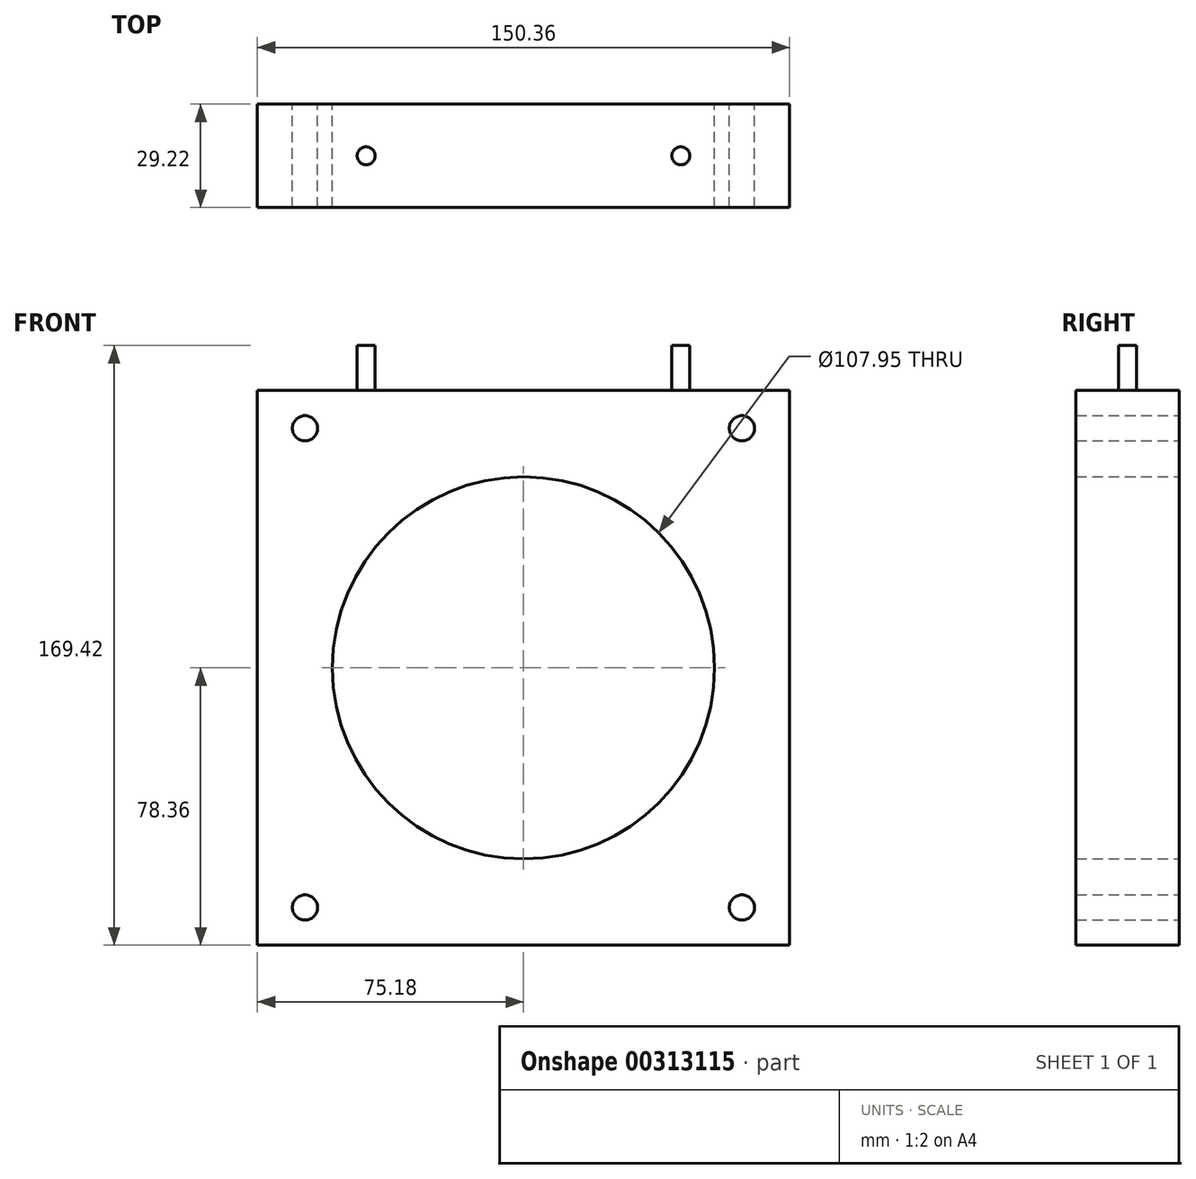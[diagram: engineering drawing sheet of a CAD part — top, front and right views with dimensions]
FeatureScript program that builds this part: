
annotation { "Feature Type Name" : "Feature", "Feature Type Description" : "" }
export const myFeature = defineFeature(function(context is Context, id is Id, definition is map)
    precondition{}
    {
        {
            var Q0;
            Q0=qCreatedBy(makeId("Front.planeOp"),FACE);
            var sketch = newSketch(context, id + "F0", { "sketchPlane" : qUnion([Q0])});
            skLineSegment(sketch, "E0.bottom", {"start": v(-75.18, 78.36) * mm, "end": v(75.18, 78.36) * mm});
            skLineSegment(sketch, "E0.top", {"start": v(-75.18, -78.36) * mm, "end": v(75.18, -78.36) * mm});
            skLineSegment(sketch, "E0.left", {"start": v(-75.18, 78.36) * mm, "end": v(-75.18, -78.36) * mm});
            skLineSegment(sketch, "E0.right", {"start": v(75.18, 78.36) * mm, "end": v(75.18, -78.36) * mm});
            skPoint(sketch, "E0.middle", {"position": v(0, 0) * mm});
            skCircle(sketch, "E1", {"center": v(-61.72, -67.7) * mm, "radius": 3.56 * mm});
            skCircle(sketch, "E2", {"center": v(61.72, -67.7) * mm, "radius": 3.56 * mm});
            skCircle(sketch, "E3", {"center": v(61.72, 67.7) * mm, "radius": 3.56 * mm});
            skCircle(sketch, "E4", {"center": v(-61.72, 67.7) * mm, "radius": 3.56 * mm});
            skLineSegment(sketch, "E5", {"start": v(-61.72, -67.7) * mm, "end": v(61.72, -67.7) * mm, "construction": true});
            skPoint(sketch, "E6", {"position": v(0, -67.7) * mm});
            skPoint(sketch, "E7", {"position": v(0, -78.36) * mm});
            skCircle(sketch, "E8", {"center": v(0, 0) * mm, "radius": 53.98 * mm});
            skSolve(sketch);
        }
        {
            var Q0;
            Q0 = qSketchRegion(id + "F0", true);
            extrude(context, id + "F1", {"entities" : qUnion([Q0]), "endBound" : BoundingType.SYMMETRIC, "depth" : 29.2 * mm});
        }
        {
            var Q0;
            Q0=makeQuery(id+"F1.opExtrude","SWEPT_FACE",FACE,{"disambiguationData":[OSD([sQuery(id+"F0.wireOp",EDGE,"E0.bottom")])]});
            var sketch = newSketch(context, id + "F2", { "sketchPlane" : qUnion([Q0])});
            skCircle(sketch, "E9", {"center": v(-44.45, 0) * mm, "radius": 2.54 * mm});
            skPoint(sketch, "E9.centerSnap0", {"position": v(-75.18, 0) * mm});
            skCircle(sketch, "E10", {"center": v(44.45, 0) * mm, "radius": 2.54 * mm});
            skLineSegment(sketch, "E11", {"start": v(-44.45, 0) * mm, "end": v(44.45, 0) * mm, "construction": true});
            skPoint(sketch, "E12", {"position": v(0, 0) * mm});
            skSolve(sketch);
        }
        {
            var Q0;
            Q0 = qSketchRegion(id + "F2", true);
            extrude(context, id + "F3", {"entities" : qUnion([Q0]), "operationType" : NewBodyOperationType.ADD, "depth" : 12.7 * mm});
        }
    });
